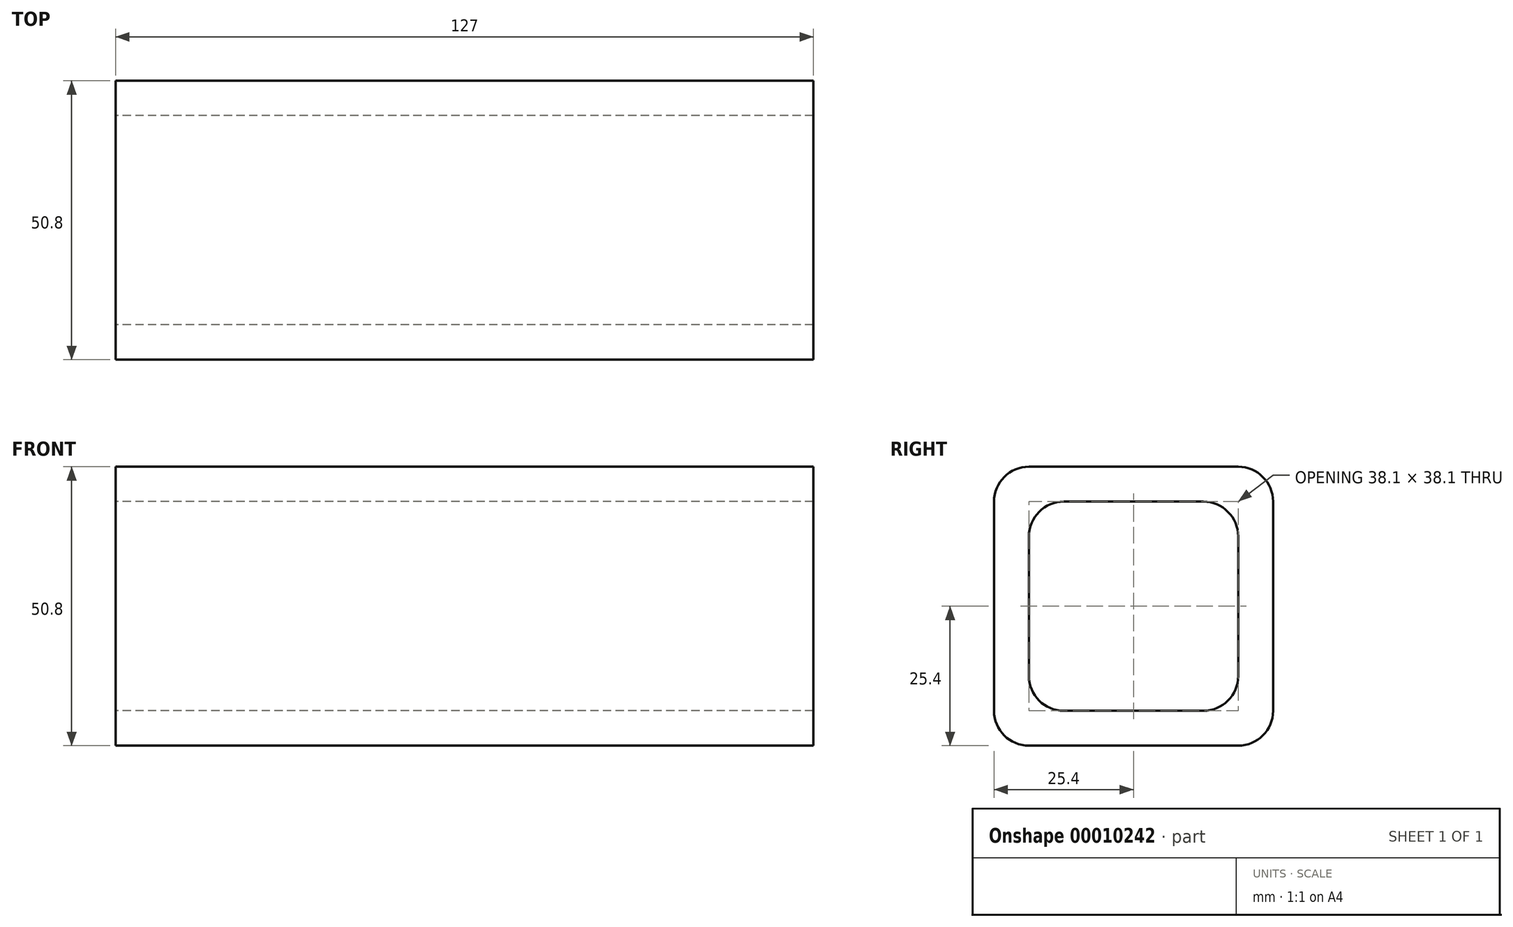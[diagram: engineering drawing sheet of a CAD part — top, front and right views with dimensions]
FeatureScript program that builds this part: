
annotation { "Feature Type Name" : "Feature", "Feature Type Description" : "" }
export const myFeature = defineFeature(function(context is Context, id is Id, definition is map)
    precondition{}
    {
        {
            var Q0;
            Q0=qCreatedBy(makeId("Right.planeOp"),FACE);
            var sketch = newSketch(context, id + "F0", { "sketchPlane" : qUnion([Q0])});
            skLineSegment(sketch, "E0.bottom", {"start": v(6.35, 50.8) * mm, "end": v(44.45, 50.8) * mm});
            skLineSegment(sketch, "E0.top", {"start": v(6.35, 0) * mm, "end": v(44.45, 0) * mm});
            skLineSegment(sketch, "E0.left", {"start": v(0, 44.45) * mm, "end": v(0, 6.35) * mm});
            skLineSegment(sketch, "E0.right", {"start": v(50.8, 44.45) * mm, "end": v(50.8, 6.35) * mm});
            skPoint(sketch, "E1.visualSharp", {"position": v(0, 50.8) * mm});
            skArc(sketch, "E1.filletArc", {"start": v(6.35, 50.8) * mm, "mid": v(1.86, 48.94) * mm, "end": v(0, 44.45) * mm});
            skPoint(sketch, "E2.visualSharp", {"position": v(0, 0) * mm});
            skArc(sketch, "E2.filletArc", {"start": v(0, 6.35) * mm, "mid": v(1.86, 1.86) * mm, "end": v(6.35, 0) * mm});
            skPoint(sketch, "E3.visualSharp", {"position": v(50.8, 0) * mm});
            skArc(sketch, "E3.filletArc", {"start": v(44.45, 0) * mm, "mid": v(48.94, 1.86) * mm, "end": v(50.8, 6.35) * mm});
            skPoint(sketch, "E4.visualSharp", {"position": v(50.8, 50.8) * mm});
            skArc(sketch, "E4.filletArc", {"start": v(50.8, 44.45) * mm, "mid": v(48.94, 48.94) * mm, "end": v(44.45, 50.8) * mm});
            skLineSegment(sketch, "E5", {"start": v(6.35, 38.1) * mm, "end": v(6.35, 12.7) * mm});
            skLineSegment(sketch, "E6", {"start": v(12.7, 6.35) * mm, "end": v(38.1, 6.35) * mm});
            skLineSegment(sketch, "E7", {"start": v(44.45, 12.7) * mm, "end": v(44.45, 38.1) * mm});
            skLineSegment(sketch, "E8", {"start": v(38.1, 44.45) * mm, "end": v(12.7, 44.45) * mm});
            skPoint(sketch, "E9.newPointA", {"position": v(6.35, 38.18) * mm});
            skArc(sketch, "E9.filletArc", {"start": v(12.7, 44.45) * mm, "mid": v(8.2, 42.6) * mm, "end": v(6.35, 38.1) * mm});
            skArc(sketch, "E10.filletArc", {"start": v(44.45, 38.1) * mm, "mid": v(42.6, 42.6) * mm, "end": v(38.1, 44.45) * mm});
            skArc(sketch, "E11.filletArc", {"start": v(38.1, 6.35) * mm, "mid": v(42.6, 8.2) * mm, "end": v(44.45, 12.7) * mm});
            skArc(sketch, "E12.filletArc", {"start": v(6.35, 12.7) * mm, "mid": v(8.2, 8.2) * mm, "end": v(12.7, 6.35) * mm});
            skSolve(sketch);
        }
        {
            var Q0;
            Q0=makeQuery(id+"F0.imprint","IMPRINT",FACE,{"disambiguationData":[TD([[makeQuery(id+"F0.imprint","IMPRINT",EDGE,{"derivedFrom":sQuery(id+"F0.wireOp",EDGE,"E0.bottom")}),-1.0]])]});
            extrude(context, id + "F1", {"entities" : qUnion([Q0]), "depth" : 127 * mm});
        }
    });
